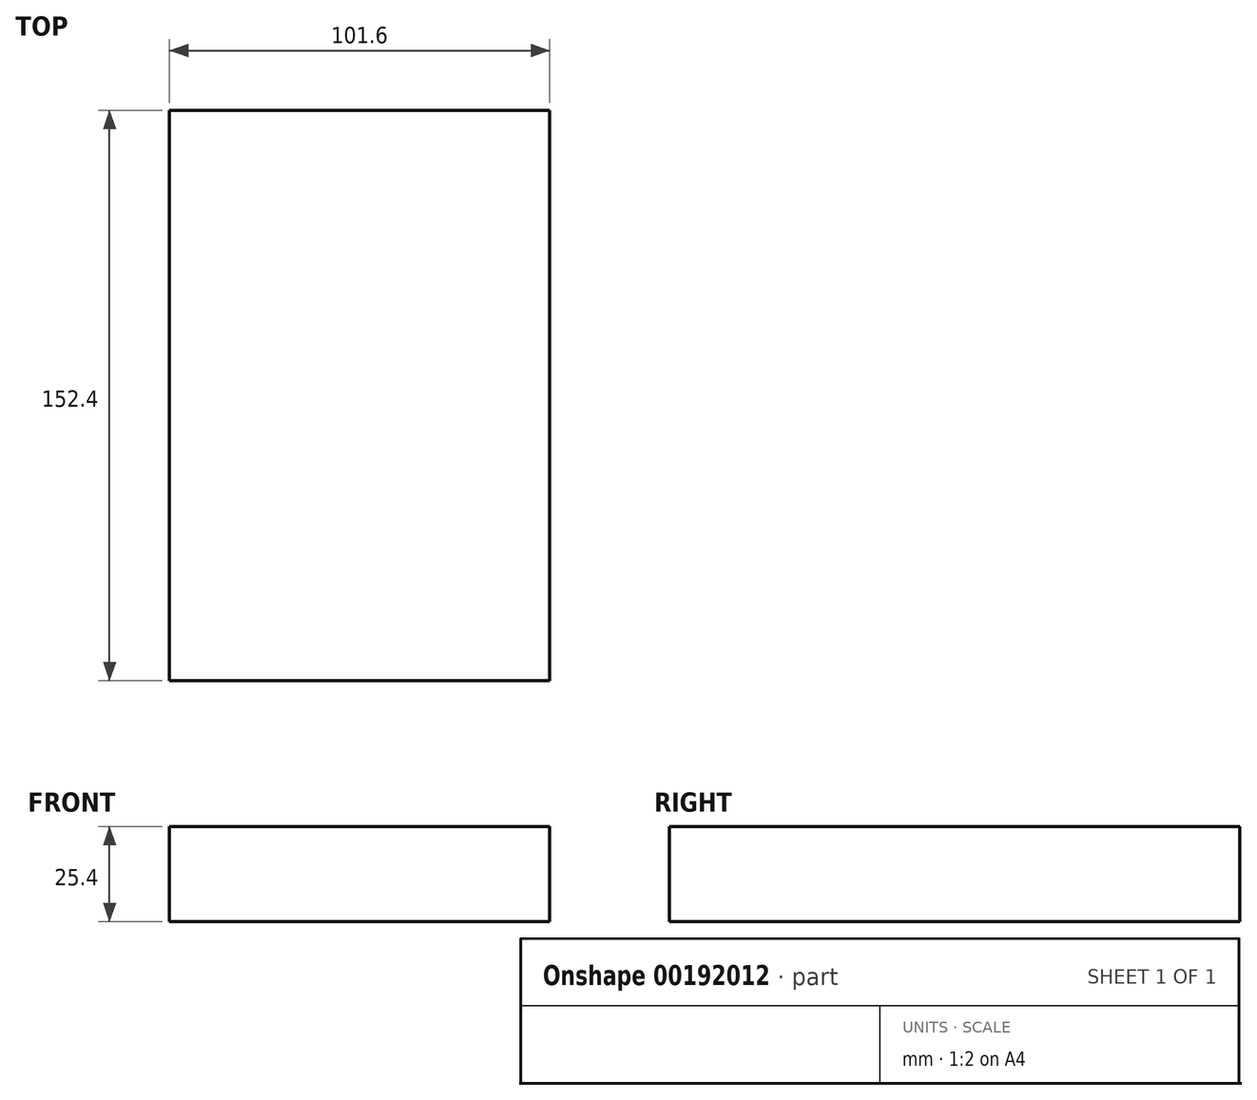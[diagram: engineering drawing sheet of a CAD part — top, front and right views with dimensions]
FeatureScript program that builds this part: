
annotation { "Feature Type Name" : "Feature", "Feature Type Description" : "" }
export const myFeature = defineFeature(function(context is Context, id is Id, definition is map)
    precondition{}
    {
        {
            var Q0;
            Q0=qCreatedBy(makeId("Top.planeOp"),FACE);
            var sketch = newSketch(context, id + "F0", { "sketchPlane" : qUnion([Q0])});
            skLineSegment(sketch, "E0.bottom", {"start": v(0, 0) * mm, "end": v(101.6, 0) * mm});
            skLineSegment(sketch, "E0.top", {"start": v(0, 152.4) * mm, "end": v(101.6, 152.4) * mm});
            skLineSegment(sketch, "E0.left", {"start": v(0, 0) * mm, "end": v(0, 152.4) * mm});
            skLineSegment(sketch, "E0.right", {"start": v(101.6, 0) * mm, "end": v(101.6, 152.4) * mm});
            skSolve(sketch);
        }
        {
            var Q0;
            Q0 = qSketchRegion(id + "F0", true);
            extrude(context, id + "F1", {"entities" : qUnion([Q0]), "depth" : 25.4 * mm});
        }
    });
